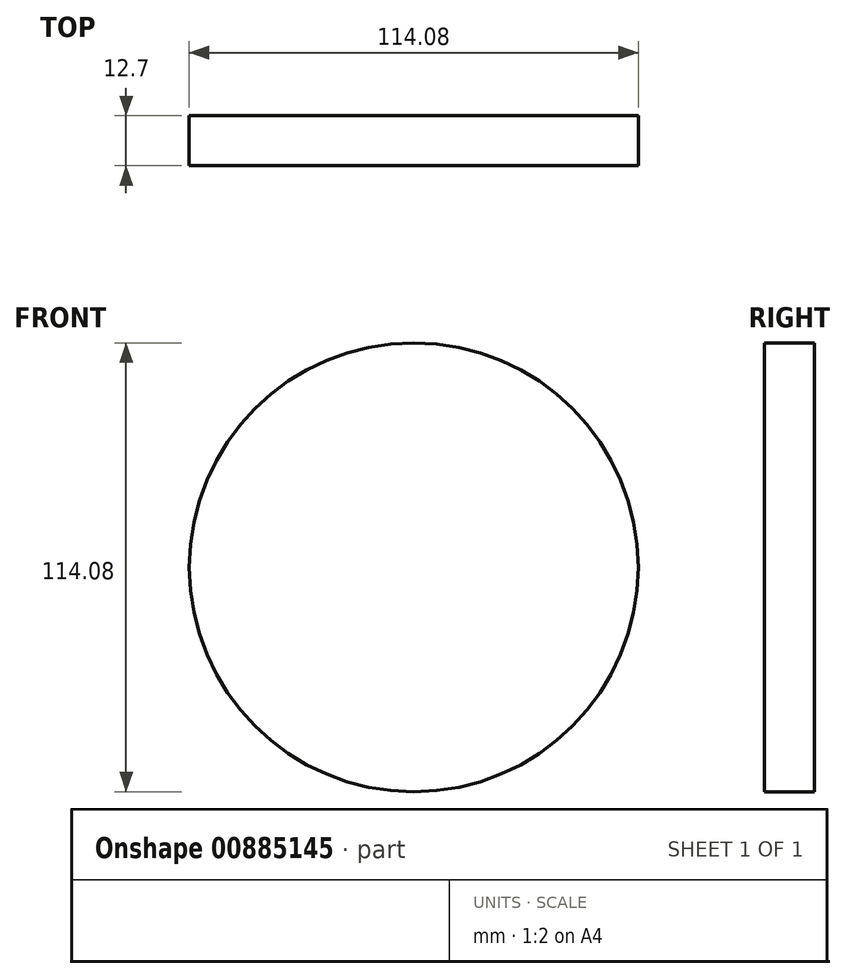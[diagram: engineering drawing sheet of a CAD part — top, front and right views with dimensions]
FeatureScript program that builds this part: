
annotation { "Feature Type Name" : "Feature", "Feature Type Description" : "" }
export const myFeature = defineFeature(function(context is Context, id is Id, definition is map)
    precondition{}
    {
        {
            var Q0;
            Q0=qCreatedBy(makeId("Front.planeOp"),FACE);
            var sketch = newSketch(context, id + "F0", { "sketchPlane" : qUnion([Q0])});
            skCircle(sketch, "E0", {"center": v(0, 0) * mm, "radius": 57.04 * mm});
            skSolve(sketch);
        }
        {
            var Q0;
            Q0=makeQuery(id+"F0.imprint","IMPRINT",FACE,{"disambiguationData":[TD([[makeQuery(id+"F0.imprint","IMPRINT",EDGE,{"derivedFrom":sQuery(id+"F0.wireOp",EDGE,"E0")}),1.0]])]});
            extrude(context, id + "F1", {"entities" : qUnion([Q0]), "depth" : 12.7 * mm, "offsetDistance" : 25.4 * mm});
        }
    });
